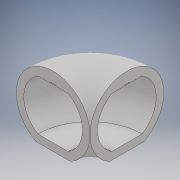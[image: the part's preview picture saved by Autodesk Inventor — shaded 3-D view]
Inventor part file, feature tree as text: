
AUTODESK INVENTOR PART (.ipt)
format: ipt  version: 2017 (Build 210142000, 142)  size: 222,208 bytes
history: native  units: in
note: dims shown in document units (in); Inventor stores cm internally (conversion verified against a paired STEP export)
features: other x2, sketch x2
ambient origin geometry x8: Origin, YZ Plane, XZ Plane, XY Plane, X Axis, Y Axis, Z Axis, Center Point
bodies: Solid1 (feature_tree), Solid2 (feature_tree)
feature tree (4):
  other  "corridor"
  other  "light"
  sketch  "Sketch1"  dims[d1=4.0in]
  sketch  "Sketch4"  dims[d2=90.0deg d11=1.0in d16=0.5833in d17=0.0625in d18=0.0625in d19=0.125in d20=0.25in d21=0.125in d22=45.0deg d23=0.0892in d24=0.0884in d25=90.0deg]
